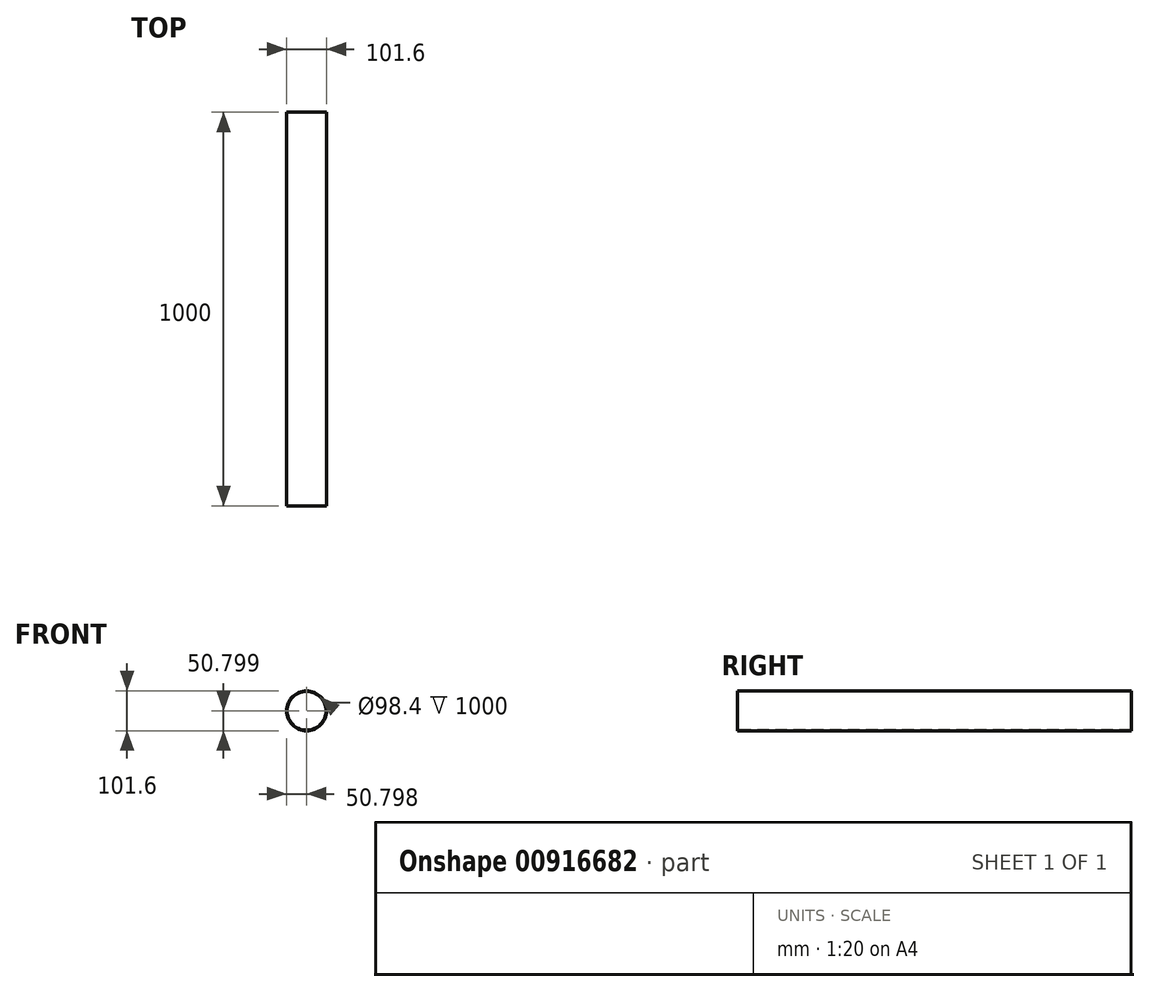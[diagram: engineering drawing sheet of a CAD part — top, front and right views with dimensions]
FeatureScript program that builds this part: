
annotation { "Feature Type Name" : "Feature", "Feature Type Description" : "" }
export const myFeature = defineFeature(function(context is Context, id is Id, definition is map)
    precondition{}
    {
        {
            var Q0;
            Q0=qCreatedBy(makeId("Front.planeOp"),FACE);
            var sketch = newSketch(context, id + "F0", { "sketchPlane" : qUnion([Q0])});
            skCircle(sketch, "E0", {"center": v(-57.45, 54.4) * mm, "radius": 50.8 * mm});
            skCircle(sketch, "E1", {"center": v(-57.45, 54.4) * mm, "radius": 49.2 * mm});
            skSolve(sketch);
        }
        {
            var Q0;
            Q0 = qSketchRegion(id + "F0", true);
            extrude(context, id + "F1", {"entities" : qUnion([Q0]), "oppositeDirection" : true, "depth" : 1000 * mm, "offsetDistance" : 25 * mm});
        }
    });
